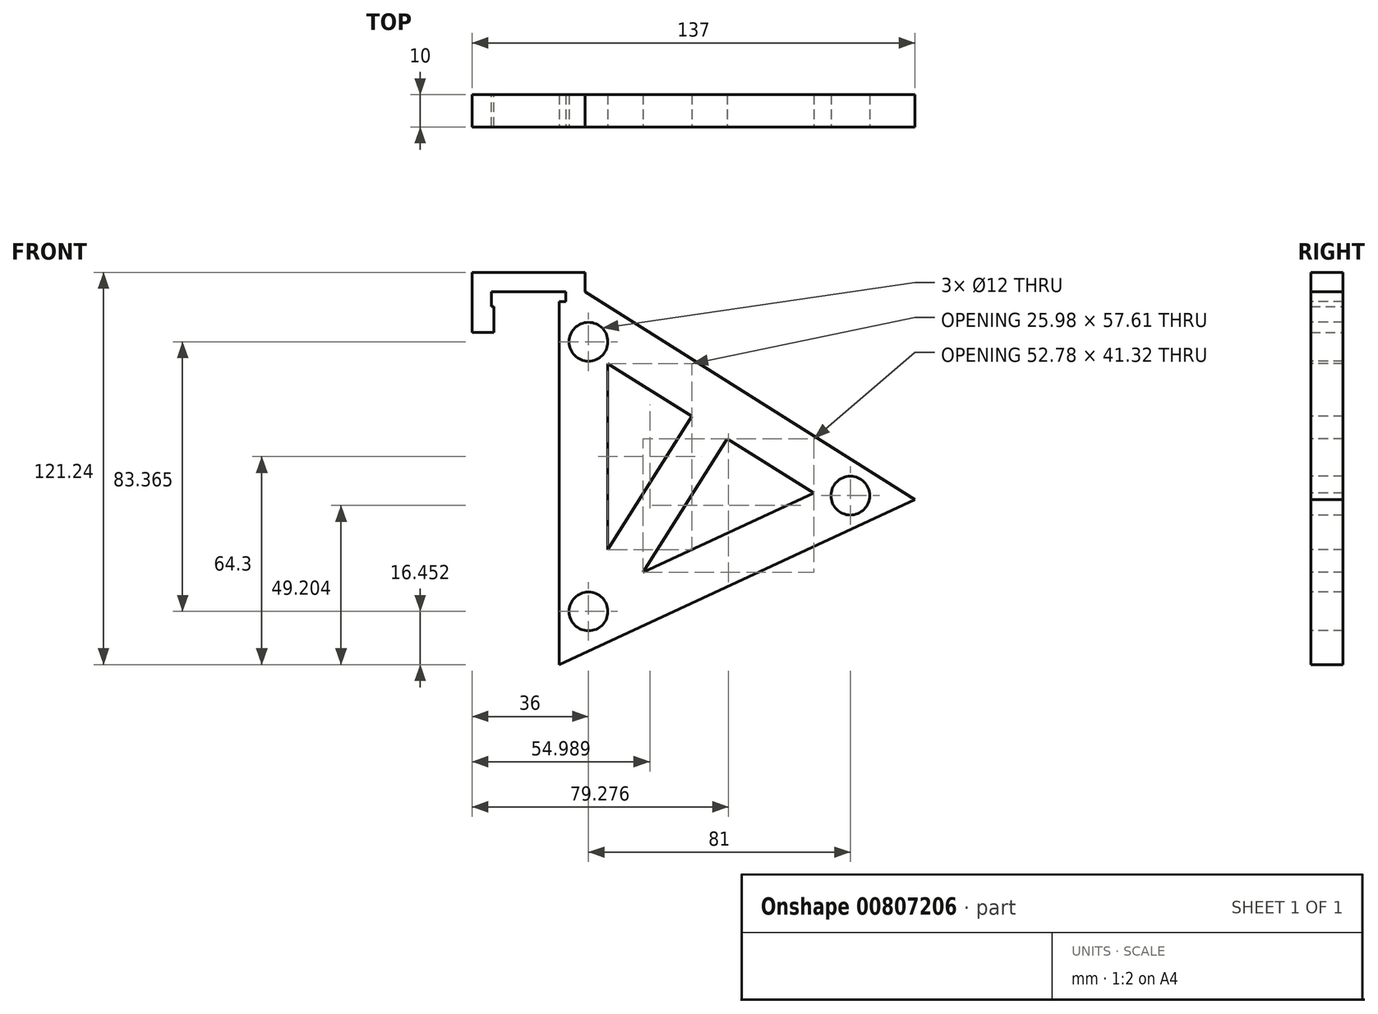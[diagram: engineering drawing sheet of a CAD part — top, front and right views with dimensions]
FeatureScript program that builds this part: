
annotation { "Feature Type Name" : "Feature", "Feature Type Description" : "" }
export const myFeature = defineFeature(function(context is Context, id is Id, definition is map)
    precondition{}
    {
        {
            var Q0;
            Q0=qCreatedBy(makeId("Front.planeOp"),FACE);
            var sketch = newSketch(context, id + "F0", { "sketchPlane" : qUnion([Q0])});
            skLineSegment(sketch, "E0", {"start": v(0, 0) * mm, "end": v(0, 12.5) * mm});
            skLineSegment(sketch, "E1", {"start": v(0, 12.5) * mm, "end": v(21, 12.5) * mm});
            skLineSegment(sketch, "E2", {"start": v(21, 12.5) * mm, "end": v(21, -102.74) * mm});
            skLineSegment(sketch, "E3", {"start": v(21, -102.74) * mm, "end": v(131, -51.73) * mm});
            skLineSegment(sketch, "E4", {"start": v(131, -51.73) * mm, "end": v(29, 12.5) * mm});
            skLineSegment(sketch, "E5", {"start": v(29, 12.5) * mm, "end": v(29, 18.5) * mm});
            skLineSegment(sketch, "E6", {"start": v(29, 18.5) * mm, "end": v(-6, 18.5) * mm});
            skLineSegment(sketch, "E7", {"start": v(-6, 18.5) * mm, "end": v(-6, 0) * mm});
            skLineSegment(sketch, "E8", {"start": v(-6, 0) * mm, "end": v(0, 0) * mm});
            skLineSegment(sketch, "E9", {"start": v(0.75, 6.25) * mm, "end": v(0.75, 0) * mm});
            skLineSegment(sketch, "E10", {"start": v(0.75, 0) * mm, "end": v(0, 0) * mm});
            skLineSegment(sketch, "E11", {"start": v(0, 8) * mm, "end": v(0.75, 8) * mm});
            skLineSegment(sketch, "E12", {"start": v(0.75, 6.25) * mm, "end": v(0.75, 8) * mm});
            skSolve(sketch);
        }
        {
            var Q0;
            {var subQ0=sQuery(id+"F0.wireOp",EDGE,"E1");Q0=makeQuery(id+"F0.imprint","IMPRINT",FACE,{"disambiguationData":[TD([[makeQuery(id+"F0.imprint","IMPRINT",EDGE,{"derivedFrom":subQ0}),1.0]])]});}
            var Q1;
            Q1=makeQuery(id+"F0.imprint","IMPRINT",FACE,{"disambiguationData":[TD([[makeQuery(id+"F0.imprint","IMPRINT",EDGE,{"derivedFrom":sQuery(id+"F0.wireOp",EDGE,"E9")}),-1.0]])]});
            extrude(context, id + "F1", {"entities" : qUnion([Q0, Q1]), "depth" : 10 * mm, "offsetDistance" : 25 * mm});
        }
        {
            var Q0;
            Q0=makeQuery(id+"F1.opExtrude","CAP_FACE",FACE,{"disambiguationData":[OSD([sQuery(id+"F0.wireOp",EDGE,"E0"),sQuery(id+"F0.wireOp",EDGE,"E1"),sQuery(id+"F0.wireOp",EDGE,"E2"),sQuery(id+"F0.wireOp",EDGE,"E3"),sQuery(id+"F0.wireOp",EDGE,"E4"),sQuery(id+"F0.wireOp",EDGE,"E5"),sQuery(id+"F0.wireOp",EDGE,"E6"),sQuery(id+"F0.wireOp",EDGE,"E7"),sQuery(id+"F0.wireOp",EDGE,"E8"),sQuery(id+"F0.wireOp",EDGE,"E9"),sQuery(id+"F0.wireOp",EDGE,"E10"),sQuery(id+"F0.wireOp",EDGE,"E11"),sQuery(id+"F0.wireOp",EDGE,"E12")])],"isStart":false});
            var sketch = newSketch(context, id + "F2", { "sketchPlane" : qUnion([Q0])});
            skLineSegment(sketch, "E13", {"start": v(36, -9.63) * mm, "end": v(36, -79.25) * mm});
            skLineSegment(sketch, "E14", {"start": v(36, -79.25) * mm, "end": v(99.67, -49.72) * mm});
            skLineSegment(sketch, "E15", {"start": v(99.67, -49.72) * mm, "end": v(36, -9.63) * mm});
            skLineSegment(sketch, "E16", {"start": v(36, -67.25) * mm, "end": v(61.98, -26) * mm});
            skLineSegment(sketch, "E17", {"start": v(46.89, -74.2) * mm, "end": v(72.9, -32.87) * mm});
            skSolve(sketch);
        }
        {
            var Q0;
            {var subQ3=sQuery(id+"F2.wireOp",EDGE,"E16");Q0=makeQuery(id+"F2.imprint","IMPRINT",FACE,{"disambiguationData":[TD([[makeQuery(id+"F2.imprint","IMPRINT",EDGE,{"derivedFrom":subQ3}),1.0]])]});}
            var Q1;
            {var subQ3=sQuery(id+"F2.wireOp",EDGE,"E17");Q1=makeQuery(id+"F2.imprint","IMPRINT",FACE,{"disambiguationData":[TD([[makeQuery(id+"F2.imprint","IMPRINT",EDGE,{"derivedFrom":subQ3}),-1.0]])]});}
            extrude(context, id + "F3", {"entities" : qUnion([Q0, Q1]), "operationType" : NewBodyOperationType.REMOVE, "oppositeDirection" : true, "depth" : 25 * mm, "offsetDistance" : 25 * mm});
        }
        {
            var Q0;
            Q0=makeQuery(id+"F1.opExtrude","CAP_FACE",FACE,{"disambiguationData":[OSD([sQuery(id+"F0.wireOp",EDGE,"E0"),sQuery(id+"F0.wireOp",EDGE,"E1"),sQuery(id+"F0.wireOp",EDGE,"E2"),sQuery(id+"F0.wireOp",EDGE,"E3"),sQuery(id+"F0.wireOp",EDGE,"E4"),sQuery(id+"F0.wireOp",EDGE,"E5"),sQuery(id+"F0.wireOp",EDGE,"E6"),sQuery(id+"F0.wireOp",EDGE,"E7"),sQuery(id+"F0.wireOp",EDGE,"E8"),sQuery(id+"F0.wireOp",EDGE,"E9"),sQuery(id+"F0.wireOp",EDGE,"E10"),sQuery(id+"F0.wireOp",EDGE,"E11"),sQuery(id+"F0.wireOp",EDGE,"E12")])],"isStart":false});
            var sketch = newSketch(context, id + "F4", { "sketchPlane" : qUnion([Q0])});
            skCircle(sketch, "E18", {"center": v(30, -2.92) * mm, "radius": 6 * mm});
            skCircle(sketch, "E19", {"center": v(30, -86.29) * mm, "radius": 6 * mm});
            skCircle(sketch, "E20", {"center": v(111, -50.5) * mm, "radius": 6 * mm});
            skSolve(sketch);
        }
        {
            var Q0;
            Q0=makeQuery(id+"F4.imprint","IMPRINT",FACE,{"disambiguationData":[TD([[makeQuery(id+"F4.imprint","IMPRINT",EDGE,{"derivedFrom":sQuery(id+"F4.wireOp",EDGE,"E18")}),1.0]])]});
            var Q1;
            Q1=makeQuery(id+"F4.imprint","IMPRINT",FACE,{"disambiguationData":[TD([[makeQuery(id+"F4.imprint","IMPRINT",EDGE,{"derivedFrom":sQuery(id+"F4.wireOp",EDGE,"E20")}),1.0]])]});
            var Q2;
            Q2=makeQuery(id+"F4.imprint","IMPRINT",FACE,{"disambiguationData":[TD([[makeQuery(id+"F4.imprint","IMPRINT",EDGE,{"derivedFrom":sQuery(id+"F4.wireOp",EDGE,"E19")}),1.0]])]});
            extrude(context, id + "F5", {"entities" : qUnion([Q0, Q1, Q2]), "operationType" : NewBodyOperationType.REMOVE, "oppositeDirection" : true, "depth" : 25 * mm, "offsetDistance" : 25 * mm});
        }
        {
            var Q0;
            Q0=makeQuery(id+"F1.opExtrude","CAP_FACE",FACE,{"disambiguationData":[OSD([sQuery(id+"F0.wireOp",EDGE,"E0"),sQuery(id+"F0.wireOp",EDGE,"E1"),sQuery(id+"F0.wireOp",EDGE,"E2"),sQuery(id+"F0.wireOp",EDGE,"E3"),sQuery(id+"F0.wireOp",EDGE,"E4"),sQuery(id+"F0.wireOp",EDGE,"E5"),sQuery(id+"F0.wireOp",EDGE,"E6"),sQuery(id+"F0.wireOp",EDGE,"E7"),sQuery(id+"F0.wireOp",EDGE,"E8"),sQuery(id+"F0.wireOp",EDGE,"E9"),sQuery(id+"F0.wireOp",EDGE,"E10"),sQuery(id+"F0.wireOp",EDGE,"E11"),sQuery(id+"F0.wireOp",EDGE,"E12")])],"isStart":false});
            var sketch = newSketch(context, id + "F6", { "sketchPlane" : qUnion([Q0])});
            skLineSegment(sketch, "E21", {"start": v(21, 12.5) * mm, "end": v(23, 12.5) * mm});
            skLineSegment(sketch, "E22", {"start": v(23, 12.5) * mm, "end": v(23, 9.5) * mm});
            skLineSegment(sketch, "E23", {"start": v(23, 9.5) * mm, "end": v(21, 9.5) * mm});
            skSolve(sketch);
        }
        {
            var Q0;
            {var subQ0=sQuery(id+"F6.wireOp",EDGE,"E21");Q0=makeQuery(id+"F6.imprint","IMPRINT",FACE,{"disambiguationData":[TD([[makeQuery(id+"F6.imprint","IMPRINT",EDGE,{"derivedFrom":subQ0}),-1.0]])]});}
            extrude(context, id + "F7", {"entities" : qUnion([Q0]), "operationType" : NewBodyOperationType.REMOVE, "oppositeDirection" : true, "depth" : 25 * mm, "offsetDistance" : 25 * mm});
        }
    });
